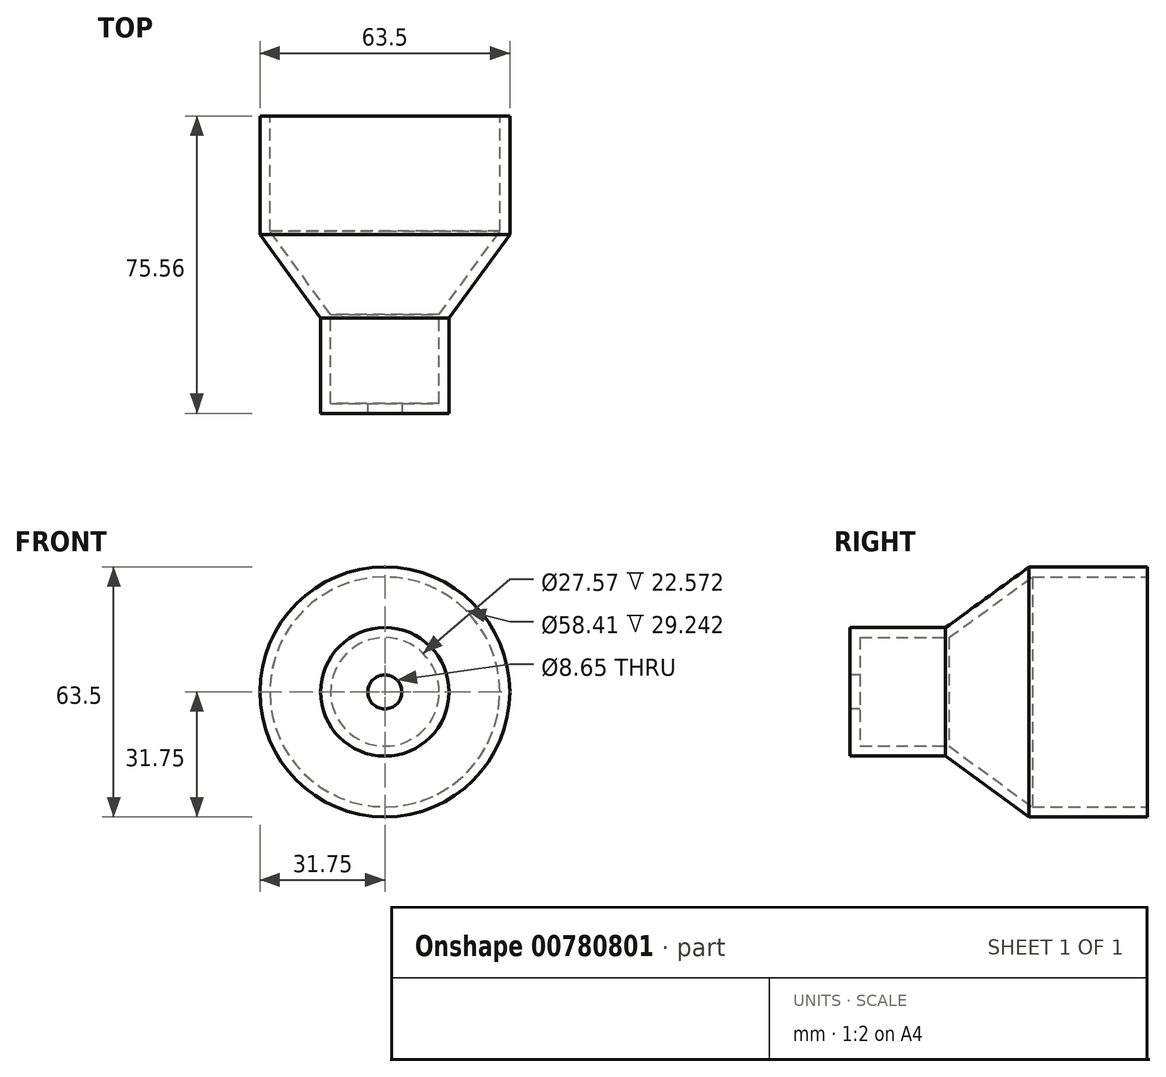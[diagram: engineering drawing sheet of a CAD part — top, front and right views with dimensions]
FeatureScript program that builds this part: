
annotation { "Feature Type Name" : "Feature", "Feature Type Description" : "" }
export const myFeature = defineFeature(function(context is Context, id is Id, definition is map)
    precondition{}
    {
        {
            var Q0;
            Q0=qCreatedBy(makeId("Top.planeOp"),FACE);
            var sketch = newSketch(context, id + "F0", { "sketchPlane" : qUnion([Q0])});
            skLineSegment(sketch, "E0", {"start": v(0, 84.74) * mm, "end": v(0, -97.98) * mm, "construction": true});
            skLineSegment(sketch, "E1", {"start": v(0, -55.19) * mm, "end": v(16.33, -55.19) * mm});
            skLineSegment(sketch, "E2", {"start": v(16.33, -55.19) * mm, "end": v(16.33, -30.9) * mm});
            skLineSegment(sketch, "E3", {"start": v(16.33, -30.9) * mm, "end": v(31.75, -9.7) * mm});
            skLineSegment(sketch, "E4", {"start": v(31.75, -9.7) * mm, "end": v(31.75, 20.37) * mm});
            skLineSegment(sketch, "E5", {"start": v(31.75, 20.37) * mm, "end": v(0, 20.37) * mm});
            skLineSegment(sketch, "E6", {"start": v(0, 20.37) * mm, "end": v(0, -55.19) * mm});
            skSolve(sketch);
        }
        {
            var Q0;
            Q0 = qSketchRegion(id + "F0", true);
            var Q1;
            Q1=sQuery(id+"F0.wireOp",EDGE,"E0");
            revolve(context, id + "F1", {"surfaceOperationType" : NewSurfaceOperationType.NEW, "entities" : qUnion([Q0]), "axis" : qUnion([Q1]), "revolveType" : RevolveType.FULL});
        }
        {
            var Q0;
            Q0=makeQuery(id+"F1.opRevolve","SWEPT_FACE",FACE,{"disambiguationData":[OSD([sQuery(id+"F0.wireOp",EDGE,"E1")])]});
            var sketch = newSketch(context, id + "F2", { "sketchPlane" : qUnion([Q0])});
            skCircle(sketch, "E7", {"center": v(0, 0) * mm, "radius": 4.33 * mm});
            skSolve(sketch);
        }
        {
            var Q0;
            Q0=makeQuery(id+"F1.opRevolve","SWEPT_FACE",FACE,{"disambiguationData":[OSD([sQuery(id+"F0.wireOp",EDGE,"E5")])]});
            shell(context, id + "F3", {"entities" : qUnion([Q0]), "thickness" : 2.54 * mm});
        }
        {
            var Q0;
            Q0 = qSketchRegion(id + "F2", true);
            extrude(context, id + "F4", {"entities" : qUnion([Q0]), "operationType" : NewBodyOperationType.REMOVE, "endBound" : BoundingType.THROUGH_ALL, "oppositeDirection" : true, "depth" : 25.4 * mm, "offsetDistance" : 25.4 * mm});
        }
    });
